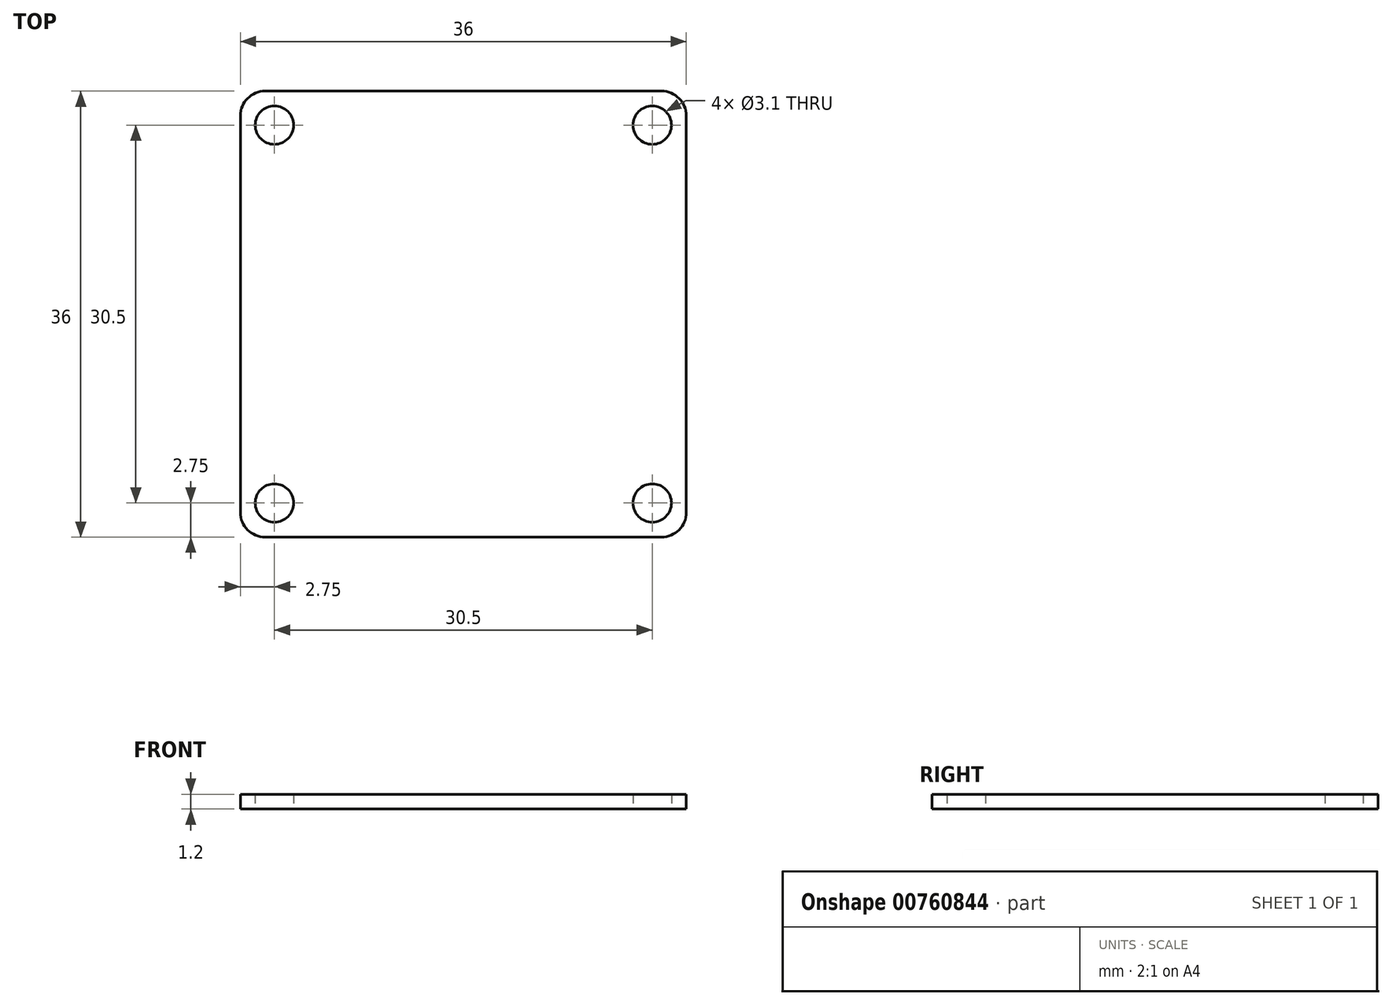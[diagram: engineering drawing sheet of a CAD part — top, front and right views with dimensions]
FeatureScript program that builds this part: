
annotation { "Feature Type Name" : "Feature", "Feature Type Description" : "" }
export const myFeature = defineFeature(function(context is Context, id is Id, definition is map)
    precondition{}
    {
        {
            var Q0;
            Q0=qCreatedBy(makeId("Top.planeOp"),FACE);
            var sketch = newSketch(context, id + "F0", { "sketchPlane" : qUnion([Q0])});
            skLineSegment(sketch, "E0.left", {"start": v(-18, 16) * mm, "end": v(-18, -16) * mm});
            skPoint(sketch, "E1.visualSharp", {"position": v(-18, 18) * mm});
            skPoint(sketch, "E2", {"position": v(-15.25, 15.25) * mm});
            skCircle(sketch, "E3", {"center": v(-15.25, 15.25) * mm, "radius": 1.55 * mm});
            skPoint(sketch, "E4", {"position": v(15.25, 15.25) * mm});
            skCircle(sketch, "E5", {"center": v(15.25, 15.25) * mm, "radius": 1.55 * mm});
            skPoint(sketch, "E6", {"position": v(15.25, -15.25) * mm});
            skPoint(sketch, "E7", {"position": v(-15.25, -15.25) * mm});
            skCircle(sketch, "E8", {"center": v(15.25, -15.25) * mm, "radius": 1.55 * mm});
            skCircle(sketch, "E9", {"center": v(-15.25, -15.25) * mm, "radius": 1.55 * mm});
            skArc(sketch, "E10.filletArc", {"start": v(-16, 18) * mm, "mid": v(-17.41, 17.41) * mm, "end": v(-18, 16) * mm});
            skLineSegment(sketch, "E11", {"start": v(-16, -18) * mm, "end": v(16, -18) * mm});
            skLineSegment(sketch, "E12", {"start": v(-16, 18) * mm, "end": v(16, 18) * mm});
            skLineSegment(sketch, "E13", {"start": v(18, 16) * mm, "end": v(18, -16) * mm});
            skPoint(sketch, "E14.visualSharp", {"position": v(18, 18) * mm});
            skArc(sketch, "E14.filletArc", {"start": v(18, 16) * mm, "mid": v(17.41, 17.41) * mm, "end": v(16, 18) * mm});
            skPoint(sketch, "E15.visualSharp", {"position": v(18, -18) * mm});
            skArc(sketch, "E15.filletArc", {"start": v(16, -18) * mm, "mid": v(17.41, -17.41) * mm, "end": v(18, -16) * mm});
            skPoint(sketch, "E16.visualSharp", {"position": v(-18, -18) * mm});
            skArc(sketch, "E16.filletArc", {"start": v(-18, -16) * mm, "mid": v(-17.41, -17.41) * mm, "end": v(-16, -18) * mm});
            skPoint(sketch, "E17", {"position": v(18, 0) * mm});
            skPoint(sketch, "E18", {"position": v(-18, 0) * mm});
            skLineSegment(sketch, "E19", {"start": v(-15.25, 15.25) * mm, "end": v(15.25, -15.25) * mm, "construction": true});
            skSolve(sketch);
        }
        {
            var Q0;
            Q0=makeQuery(id+"F0.imprint","IMPRINT",FACE,{"disambiguationData":[TD([[makeQuery(id+"F0.imprint","IMPRINT",EDGE,{"derivedFrom":sQuery(id+"F0.wireOp",EDGE,"E0.left")}),1.0]])]});
            extrude(context, id + "F1", {"entities" : qUnion([Q0]), "depth" : 1.2 * mm, "offsetDistance" : 25 * mm});
        }
    });
